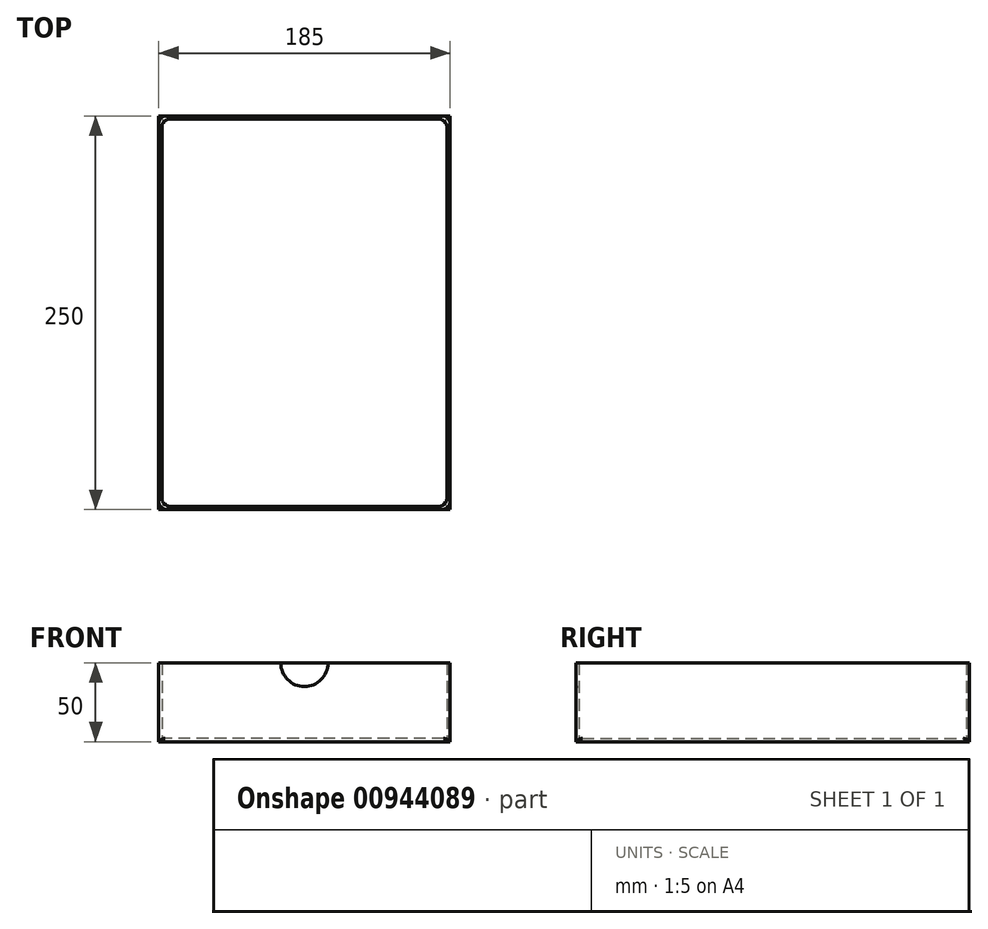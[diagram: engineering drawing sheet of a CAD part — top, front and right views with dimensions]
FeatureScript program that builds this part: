
annotation { "Feature Type Name" : "Feature", "Feature Type Description" : "" }
export const myFeature = defineFeature(function(context is Context, id is Id, definition is map)
    precondition{}
    {
        {
            var Q0;
            Q0=qCreatedBy(makeId("Top.planeOp"),FACE);
            var sketch = newSketch(context, id + "F0", { "sketchPlane" : qUnion([Q0])});
            skLineSegment(sketch, "E0.bottom", {"start": v(-92.5, 125) * mm, "end": v(92.5, 125) * mm});
            skLineSegment(sketch, "E0.top", {"start": v(-92.5, -125) * mm, "end": v(92.5, -125) * mm});
            skLineSegment(sketch, "E0.left", {"start": v(-92.5, 125) * mm, "end": v(-92.5, -125) * mm});
            skLineSegment(sketch, "E0.right", {"start": v(92.5, 125) * mm, "end": v(92.5, -125) * mm});
            skPoint(sketch, "E0.middle", {"position": v(0, 0) * mm});
            skLineSegment(sketch, "E1.bottom", {"start": v(-90.5, 123) * mm, "end": v(90.5, 123) * mm});
            skLineSegment(sketch, "E1.top", {"start": v(-90.5, -123) * mm, "end": v(90.5, -123) * mm});
            skLineSegment(sketch, "E1.left", {"start": v(-90.5, 123) * mm, "end": v(-90.5, -123) * mm});
            skLineSegment(sketch, "E1.right", {"start": v(90.5, 123) * mm, "end": v(90.5, -123) * mm});
            skSolve(sketch);
        }
        {
            var Q0;
            Q0=makeQuery(id+"F0.imprint","IMPRINT",FACE,{"disambiguationData":[TD([[makeQuery(id+"F0.imprint","IMPRINT",EDGE,{"derivedFrom":sQuery(id+"F0.wireOp",EDGE,"E0.bottom")}),-1.0]])]});
            extrude(context, id + "F1", {"entities" : qUnion([Q0]), "depth" : 50 * mm, "offsetDistance" : 25 * mm});
        }
        {
            var Q0;
            Q0 = qSketchRegion(id + "F0", true);
            var Q1;
            Q1=makeQuery(id+"F0.imprint","IMPRINT",FACE,{"disambiguationData":[TD([[makeQuery(id+"F0.imprint","IMPRINT",EDGE,{"derivedFrom":sQuery(id+"F0.wireOp",EDGE,"E1.bottom")}),-1.0]])]});
            extrude(context, id + "F2", {"entities" : qUnion([Q0, Q1]), "depth" : 2 * mm, "offsetDistance" : 25 * mm});
        }
        {
            var Q0;
            Q0=makeQuery(id+"F1.opExtrude","SWEPT_EDGE",EDGE,{"disambiguationData":[OSD([sQuery(id+"F0.wireOp",EDGE,"E0.bottom"),sQuery(id+"F0.wireOp",EDGE,"E0.right")])]});
            var Q1;
            Q1=makeQuery(id+"F1.opExtrude","SWEPT_EDGE",EDGE,{"disambiguationData":[OSD([sQuery(id+"F0.wireOp",EDGE,"E0.bottom"),sQuery(id+"F0.wireOp",EDGE,"E0.left")])]});
            var Q2;
            Q2=makeQuery(id+"F1.opExtrude","SWEPT_EDGE",EDGE,{"disambiguationData":[OSD([sQuery(id+"F0.wireOp",EDGE,"E1.bottom"),sQuery(id+"F0.wireOp",EDGE,"E1.right")])]});
            var Q3;
            Q3=makeQuery(id+"F1.opExtrude","SWEPT_EDGE",EDGE,{"disambiguationData":[OSD([sQuery(id+"F0.wireOp",EDGE,"E1.bottom"),sQuery(id+"F0.wireOp",EDGE,"E1.left")])]});
            var Q4;
            Q4=makeQuery(id+"F1.opExtrude","SWEPT_EDGE",EDGE,{"disambiguationData":[OSD([sQuery(id+"F0.wireOp",EDGE,"E1.top"),sQuery(id+"F0.wireOp",EDGE,"E1.left")])]});
            var Q5;
            Q5=makeQuery(id+"F1.opExtrude","SWEPT_EDGE",EDGE,{"disambiguationData":[OSD([sQuery(id+"F0.wireOp",EDGE,"E0.top"),sQuery(id+"F0.wireOp",EDGE,"E0.left")])]});
            var Q6;
            Q6=makeQuery(id+"F1.opExtrude","SWEPT_EDGE",EDGE,{"disambiguationData":[OSD([sQuery(id+"F0.wireOp",EDGE,"E0.top"),sQuery(id+"F0.wireOp",EDGE,"E0.right")])]});
            var Q7;
            Q7=makeQuery(id+"F1.opExtrude","SWEPT_EDGE",EDGE,{"disambiguationData":[OSD([sQuery(id+"F0.wireOp",EDGE,"E1.top"),sQuery(id+"F0.wireOp",EDGE,"E1.right")])]});
            fillet(context, id + "F3", {"entities" : qUnion([Q0, Q1, Q2, Q3, Q4, Q5, Q6, Q7]), "radius" : 5 * mm, "tangentPropagation" : true, "allowEdgeOverflow" : false});
        }
        {
            var Q0;
            Q0=makeQuery(id+"F2.opExtrude","CAP_FACE",FACE,{"disambiguationData":[OSD([sQuery(id+"F0.wireOp",EDGE,"E0.bottom"),sQuery(id+"F0.wireOp",EDGE,"E0.top"),sQuery(id+"F0.wireOp",EDGE,"E0.left"),sQuery(id+"F0.wireOp",EDGE,"E0.right")])],"isStart":false});
            fillet(context, id + "F4", {"entities" : qUnion([Q0]), "radius" : 5 * mm, "tangentPropagation" : true, "allowEdgeOverflow" : false});
        }
        {
            var Q0;
            Q0=makeQuery(id+"F1.opExtrude","SWEPT_FACE",FACE,{"disambiguationData":[OSD([sQuery(id+"F0.wireOp",EDGE,"E0.top")])]});
            var sketch = newSketch(context, id + "F5", { "sketchPlane" : qUnion([Q0])});
            skPoint(sketch, "E2", {"position": v(0, 50) * mm});
            skCircle(sketch, "E3", {"center": v(0, 50) * mm, "radius": 15 * mm});
            skSolve(sketch);
        }
        {
            var Q0;
            Q0 = qSketchRegion(id + "F5", true);
            extrude(context, id + "F6", {"entities" : qUnion([Q0]), "operationType" : NewBodyOperationType.REMOVE, "oppositeDirection" : true, "depth" : 25 * mm, "offsetDistance" : 25 * mm});
        }
        {
            var Q0;
            Q0=makeQuery(id+"F6.boolean.opBoolean","INTERSECT",EDGE,{"derivedFrom":[makeQuery(id+"F1.opExtrude","SWEPT_FACE",FACE,{"disambiguationData":[OSD([sQuery(id+"F0.wireOp",EDGE,"E1.top")])]}),makeQuery(id+"F6.opExtrude","SWEPT_FACE",FACE,{"disambiguationData":[OSD([sQuery(id+"F5.wireOp",EDGE,"E3")])]})]});
            var Q1;
            Q1=makeQuery(id+"F6.boolean.opBoolean","COPY",EDGE,{"derivedFrom":makeQuery(id+"F6.opExtrude","CAP_EDGE",EDGE,{"disambiguationData":[OSD([sQuery(id+"F5.wireOp",EDGE,"E3")])],"isStart":true})});
            fillet(context, id + "F7", {"entities" : qUnion([Q0, Q1]), "radius" : 1 * mm, "tangentPropagation" : true, "allowEdgeOverflow" : false});
        }
    });
